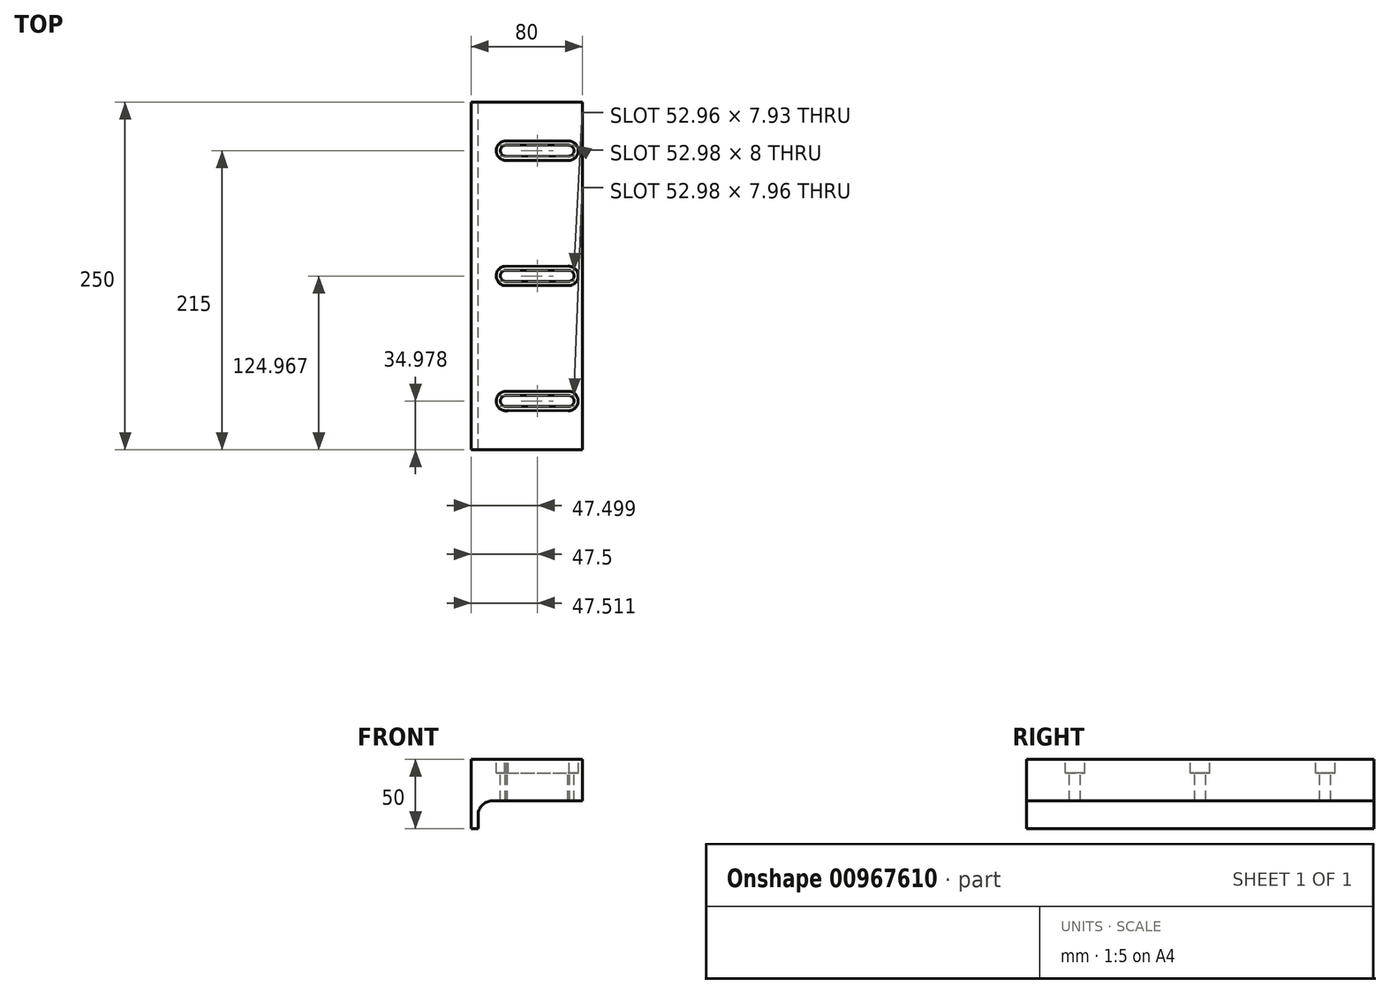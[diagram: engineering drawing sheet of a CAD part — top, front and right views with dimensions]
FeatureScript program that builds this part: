
annotation { "Feature Type Name" : "Feature", "Feature Type Description" : "" }
export const myFeature = defineFeature(function(context is Context, id is Id, definition is map)
    precondition{}
    {
        {
            var Q0;
            Q0=qCreatedBy(makeId("Front.planeOp"),FACE);
            var sketch = newSketch(context, id + "F0", { "sketchPlane" : qUnion([Q0])});
            skLineSegment(sketch, "E0.bottom", {"start": v(-40, -25) * mm, "end": v(-35, -25) * mm});
            skLineSegment(sketch, "E0.top", {"start": v(-40, 25) * mm, "end": v(40, 25) * mm});
            skLineSegment(sketch, "E0.left", {"start": v(-40, -25) * mm, "end": v(-40, 25) * mm});
            skLineSegment(sketch, "E0.right", {"start": v(40, -5) * mm, "end": v(40, 25) * mm});
            skPoint(sketch, "E0.middle", {"position": v(0, 0) * mm});
            skLineSegment(sketch, "E1", {"start": v(40, -5) * mm, "end": v(-25, -5) * mm});
            skLineSegment(sketch, "E2", {"start": v(-35, -15) * mm, "end": v(-35, -25) * mm});
            skPoint(sketch, "E3.orphan", {"position": v(40, -25) * mm});
            skPoint(sketch, "E4.visualSharp", {"position": v(-35, -5) * mm});
            skArc(sketch, "E4.filletArc", {"start": v(-25, -5) * mm, "mid": v(-32.07, -7.93) * mm, "end": v(-35, -15) * mm});
            skSolve(sketch);
        }
        {
            var Q0;
            Q0 = qSketchRegion(id + "F0", true);
            extrude(context, id + "F1", {"entities" : qUnion([Q0]), "depth" : 250 * mm, "offsetDistance" : 25 * mm});
        }
        {
            var Q0;
            Q0=makeQuery(id+"F1.opExtrude","SWEPT_FACE",FACE,{"disambiguationData":[OSD([sQuery(id+"F0.wireOp",EDGE,"E0.top")])]});
            cPlane(context, id + "F2", {"entities" : qUnion([Q0]), "cplaneType" : CPlaneType.OFFSET, "offset" : 0 * mm, "width" : 150 * mm, "height" : 150 * mm});
        }
        {
            var Q0;
            Q0=qCreatedBy(id+"F2.planeOp",FACE);
            var sketch = newSketch(context, id + "F3", { "sketchPlane" : qUnion([Q0])});
            skLineSegment(sketch, "E5", {"start": v(-55.13, -35) * mm, "end": v(71.15, -35) * mm, "construction": true});
            skLineSegment(sketch, "E6", {"start": v(-55.13, -125) * mm, "end": v(71.15, -125) * mm, "construction": true});
            skLineSegment(sketch, "E7", {"start": v(-55.51, -215) * mm, "end": v(65.81, -215) * mm, "construction": true});
            skLineSegment(sketch, "E8", {"start": v(0, 37.3) * mm, "end": v(0, -233.19) * mm, "construction": true});
            skArc(sketch, "E9", {"start": v(30, -42) * mm, "mid": v(37, -35) * mm, "end": v(30, -28) * mm});
            skArc(sketch, "E10", {"start": v(30, -132) * mm, "mid": v(37, -125) * mm, "end": v(30, -118) * mm});
            skArc(sketch, "E11", {"start": v(29.97, -222) * mm, "mid": v(37, -214.69) * mm, "end": v(29.34, -208.03) * mm});
            skArc(sketch, "E12", {"start": v(-14.95, -28) * mm, "mid": v(-22, -35.15) * mm, "end": v(-14.65, -42) * mm});
            skArc(sketch, "E13", {"start": v(-14.2, -118.05) * mm, "mid": v(-22, -125) * mm, "end": v(-14.2, -131.96) * mm});
            skArc(sketch, "E14", {"start": v(-14.34, -208.03) * mm, "mid": v(-21.98, -215.5) * mm, "end": v(-13.36, -221.8) * mm});
            skLineSegment(sketch, "E15", {"start": v(-15.05, -28) * mm, "end": v(30, -28) * mm});
            skLineSegment(sketch, "E16", {"start": v(-14.65, -42) * mm, "end": v(30, -42) * mm});
            skLineSegment(sketch, "E17", {"start": v(-15.82, -118.05) * mm, "end": v(30, -118) * mm});
            skLineSegment(sketch, "E18", {"start": v(-14.2, -131.96) * mm, "end": v(30, -132) * mm});
            skLineSegment(sketch, "E19", {"start": v(-14.34, -208.03) * mm, "end": v(30.66, -208.03) * mm});
            skLineSegment(sketch, "E20", {"start": v(-13.36, -221.8) * mm, "end": v(30, -222) * mm});
            skSolve(sketch);
        }
        {
            var Q0;
            {var subQ4=sQuery(id+"F3.wireOp",EDGE,"E10");Q0=makeQuery(id+"F3.imprint","IMPRINT",FACE,{"disambiguationData":[TD([[makeQuery(id+"F3.imprint","IMPRINT",EDGE,{"derivedFrom":subQ4}),1.0]])]});}
            var Q1;
            {var subQ4=sQuery(id+"F3.wireOp",EDGE,"E14");Q1=makeQuery(id+"F3.imprint","IMPRINT",FACE,{"disambiguationData":[TD([[makeQuery(id+"F3.imprint","IMPRINT",EDGE,{"derivedFrom":subQ4}),1.0]])]});}
            var Q2;
            {var subQ3=sQuery(id+"F3.wireOp",EDGE,"E9");Q2=makeQuery(id+"F3.imprint","IMPRINT",FACE,{"disambiguationData":[TD([[makeQuery(id+"F3.imprint","IMPRINT",EDGE,{"derivedFrom":subQ3}),1.0]])]});}
            extrude(context, id + "F4", {"entities" : qUnion([Q0, Q1, Q2]), "operationType" : NewBodyOperationType.REMOVE, "oppositeDirection" : true, "depth" : 10 * mm, "offsetDistance" : 25 * mm});
        }
        {
            var Q0;
            Q0=qCreatedBy(id+"F2.planeOp",FACE);
            var sketch = newSketch(context, id + "F5", { "sketchPlane" : qUnion([Q0])});
            skLineSegment(sketch, "E21", {"start": v(-4.05, -35) * mm, "end": v(48.8, -35) * mm, "construction": true});
            skLineSegment(sketch, "E22", {"start": v(0, -125) * mm, "end": v(49.05, -125) * mm, "construction": true});
            skLineSegment(sketch, "E23", {"start": v(0, -215) * mm, "end": v(54.36, -215) * mm, "construction": true});
            skArc(sketch, "E24", {"start": v(30, -39) * mm, "mid": v(34, -35) * mm, "end": v(30, -31) * mm});
            skArc(sketch, "E25", {"start": v(-14.83, -31) * mm, "mid": v(-19, -35.24) * mm, "end": v(-14.34, -38.95) * mm});
            skArc(sketch, "E26", {"start": v(29.82, -129) * mm, "mid": v(33.98, -124.6) * mm, "end": v(29.04, -121.12) * mm});
            skArc(sketch, "E27", {"start": v(-14.04, -121.12) * mm, "mid": v(-18.98, -124.6) * mm, "end": v(-14.82, -129) * mm});
            skArc(sketch, "E28", {"start": v(30, -219) * mm, "mid": v(33.99, -214.7) * mm, "end": v(29.41, -211.04) * mm});
            skArc(sketch, "E29", {"start": v(-14.41, -211.04) * mm, "mid": v(-19, -214.73) * mm, "end": v(-14.95, -219) * mm});
            skLineSegment(sketch, "E30", {"start": v(-14.41, -211.04) * mm, "end": v(29.41, -211.04) * mm});
            skLineSegment(sketch, "E31", {"start": v(-14.95, -219) * mm, "end": v(30, -219) * mm});
            skLineSegment(sketch, "E32", {"start": v(-14.82, -129) * mm, "end": v(30.18, -129) * mm});
            skLineSegment(sketch, "E33", {"start": v(-14.04, -121.12) * mm, "end": v(30.96, -121.12) * mm});
            skLineSegment(sketch, "E34", {"start": v(-14.83, -31) * mm, "end": v(30, -31) * mm});
            skLineSegment(sketch, "E35", {"start": v(-15.67, -38.94) * mm, "end": v(30, -39) * mm});
            skSolve(sketch);
        }
        {
            var Q0;
            Q0=makeQuery(id+"F5.imprint","IMPRINT",FACE,{"disambiguationData":[TD([[makeQuery(id+"F5.imprint","IMPRINT",EDGE,{"derivedFrom":sQuery(id+"F5.wireOp",EDGE,"E28")}),1.0]])]});
            var Q1;
            {var subQ4=sQuery(id+"F5.wireOp",EDGE,"E27");Q1=makeQuery(id+"F5.imprint","IMPRINT",FACE,{"disambiguationData":[TD([[makeQuery(id+"F5.imprint","IMPRINT",EDGE,{"derivedFrom":subQ4}),1.0]])]});}
            var Q2;
            {var subQ5=sQuery(id+"F5.wireOp",EDGE,"E24");Q2=makeQuery(id+"F5.imprint","IMPRINT",FACE,{"disambiguationData":[TD([[makeQuery(id+"F5.imprint","IMPRINT",EDGE,{"derivedFrom":subQ5}),1.0]])]});}
            extrude(context, id + "F6", {"entities" : qUnion([Q0, Q1, Q2]), "operationType" : NewBodyOperationType.REMOVE, "oppositeDirection" : true, "depth" : 108 * mm, "offsetDistance" : 25 * mm});
        }
    });
